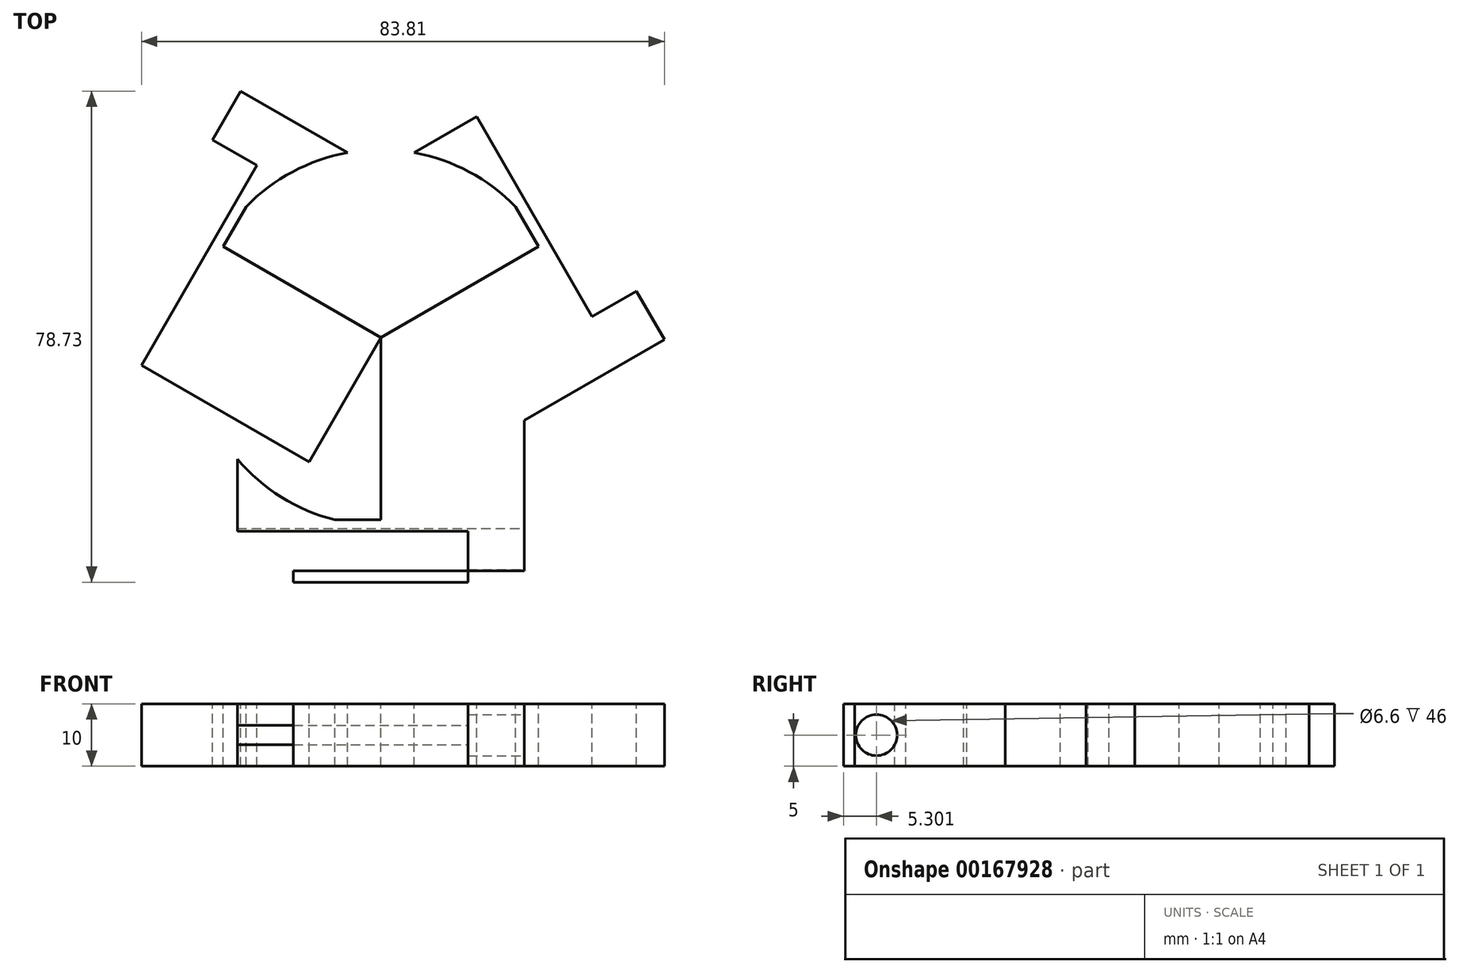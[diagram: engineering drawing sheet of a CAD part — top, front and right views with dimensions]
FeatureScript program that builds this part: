
annotation { "Feature Type Name" : "Feature", "Feature Type Description" : "" }
export const myFeature = defineFeature(function(context is Context, id is Id, definition is map)
    precondition{}
    {
        {
            var Q0;
            Q0=qCreatedBy(makeId("Top.planeOp"),FACE);
            var sketch = newSketch(context, id + "F0", { "sketchPlane" : qUnion([Q0])});
            skLineSegment(sketch, "E0", {"start": v(-23, -19.45) * mm, "end": v(-23, -31) * mm});
            skLineSegment(sketch, "E1", {"start": v(-23, -31) * mm, "end": v(-14, -31) * mm});
            skLineSegment(sketch, "E2", {"start": v(-14, -31) * mm, "end": v(-14, -29.2) * mm});
            skLineSegment(sketch, "E3", {"start": v(-23, -39.2) * mm, "end": v(-14, -39.2) * mm});
            skLineSegment(sketch, "E4", {"start": v(-14, -39.2) * mm, "end": v(-14, -37.4) * mm});
            skLineSegment(sketch, "E5", {"start": v(-14, -37.4) * mm, "end": v(-23, -37.4) * mm});
            skLineSegment(sketch, "E6", {"start": v(-23, -37.4) * mm, "end": v(-23, -39.2) * mm});
            skCircle(sketch, "E7", {"center": v(0, 0) * mm, "radius": 30.13 * mm});
            skLineSegment(sketch, "E8.bottom", {"start": v(-23, -39.2) * mm, "end": v(0, -39.2) * mm});
            skLineSegment(sketch, "E8.top", {"start": v(-23, 0) * mm, "end": v(0, 0) * mm});
            skLineSegment(sketch, "E8.left", {"start": v(-23, -39.2) * mm, "end": v(-23, 0) * mm});
            skLineSegment(sketch, "E8.right", {"start": v(0, -39.2) * mm, "end": v(0, 0) * mm});
            skLineSegment(sketch, "E9.bottom", {"start": v(-23, -31) * mm, "end": v(0, -31) * mm});
            skLineSegment(sketch, "E9.top", {"start": v(-23, -37.4) * mm, "end": v(0, -37.4) * mm});
            skLineSegment(sketch, "E9.left", {"start": v(-23, -31) * mm, "end": v(-23, -37.4) * mm});
            skLineSegment(sketch, "E9.right", {"start": v(0, -31) * mm, "end": v(0, -37.4) * mm});
            skLineSegment(sketch, "E10.bottom", {"start": v(-14, -29.2) * mm, "end": v(0, -29.2) * mm});
            skLineSegment(sketch, "E10.top", {"start": v(-14, -39.2) * mm, "end": v(0, -39.2) * mm});
            skLineSegment(sketch, "E10.left", {"start": v(-14, -29.2) * mm, "end": v(-14, -39.2) * mm});
            skLineSegment(sketch, "E10.right", {"start": v(0, -29.2) * mm, "end": v(0, -39.2) * mm});
            skLineSegment(sketch, "E11", {"start": v(-23, -34.2) * mm, "end": v(0, -34.2) * mm, "construction": true});
            skLineSegment(sketch, "E12.MirrorCS", {"start": v(23, -37.4) * mm, "end": v(23, -39.2) * mm});
            skLineSegment(sketch, "E13.MirrorCS", {"start": v(14, -39.2) * mm, "end": v(14, -37.4) * mm});
            skLineSegment(sketch, "E14.MirrorCS", {"start": v(14, -31) * mm, "end": v(14, -29.2) * mm});
            skLineSegment(sketch, "E15.MirrorCS", {"start": v(23, -31) * mm, "end": v(14, -31) * mm});
            skLineSegment(sketch, "E16.MirrorCS", {"start": v(23, -39.2) * mm, "end": v(14, -39.2) * mm});
            skLineSegment(sketch, "E17.MirrorCS", {"start": v(23, -31) * mm, "end": v(23, -37.4) * mm});
            skLineSegment(sketch, "E18.MirrorCS", {"start": v(23, -19.45) * mm, "end": v(23, -31) * mm});
            skLineSegment(sketch, "E19.MirrorCS", {"start": v(14, -37.4) * mm, "end": v(23, -37.4) * mm});
            skLineSegment(sketch, "E20.MirrorCS", {"start": v(14, -29.2) * mm, "end": v(14, -39.2) * mm});
            skLineSegment(sketch, "E21.MirrorCS", {"start": v(23, -39.2) * mm, "end": v(0, -39.2) * mm});
            skLineSegment(sketch, "E22.MirrorCS", {"start": v(23, 0) * mm, "end": v(0, 0) * mm});
            skLineSegment(sketch, "E23.MirrorCS", {"start": v(23, -37.4) * mm, "end": v(0, -37.4) * mm});
            skLineSegment(sketch, "E24.MirrorCS", {"start": v(23, -34.2) * mm, "end": v(0, -34.2) * mm, "construction": true});
            skLineSegment(sketch, "E25.MirrorCS", {"start": v(14, -39.2) * mm, "end": v(0, -39.2) * mm});
            skLineSegment(sketch, "E26.MirrorCS", {"start": v(14, -29.2) * mm, "end": v(0, -29.2) * mm});
            skLineSegment(sketch, "E27.MirrorCS", {"start": v(23, -31) * mm, "end": v(0, -31) * mm});
            skLineSegment(sketch, "E28.MirrorCS", {"start": v(23, -39.2) * mm, "end": v(23, 0) * mm});
            skLineSegment(sketch, "E29.1.0", {"start": v(33.96, 19.6) * mm, "end": v(0, 0) * mm});
            skLineSegment(sketch, "E29.1.1", {"start": v(20.9, 38.62) * mm, "end": v(32.4, 18.7) * mm});
            skLineSegment(sketch, "E29.1.2", {"start": v(22.46, 39.52) * mm, "end": v(26.96, 31.73) * mm});
            skLineSegment(sketch, "E29.1.3", {"start": v(32.3, 2.48) * mm, "end": v(40.96, 7.48) * mm});
            skLineSegment(sketch, "E29.1.4", {"start": v(-11.5, 19.92) * mm, "end": v(0, 0) * mm});
            skLineSegment(sketch, "E29.1.5", {"start": v(15.35, 35.42) * mm, "end": v(19.85, 27.63) * mm});
            skLineSegment(sketch, "E29.1.6", {"start": v(18.3, 26.73) * mm, "end": v(25.3, 14.6) * mm});
            skLineSegment(sketch, "E29.1.7", {"start": v(40.96, 7.48) * mm, "end": v(33.96, 19.6) * mm});
            skLineSegment(sketch, "E29.1.8", {"start": v(22.46, 39.52) * mm, "end": v(33.96, 19.6) * mm});
            skLineSegment(sketch, "E29.1.9", {"start": v(5.34, 29.64) * mm, "end": v(15.35, 35.42) * mm});
            skLineSegment(sketch, "E29.1.10", {"start": v(22.46, 39.52) * mm, "end": v(-11.5, 19.92) * mm});
            skLineSegment(sketch, "E29.1.11", {"start": v(32.3, 2.48) * mm, "end": v(25.3, 14.6) * mm});
            skLineSegment(sketch, "E29.1.12", {"start": v(18.3, 26.73) * mm, "end": v(26.96, 31.73) * mm});
            skLineSegment(sketch, "E29.1.13", {"start": v(15.35, 35.42) * mm, "end": v(26.85, 15.5) * mm});
            skLineSegment(sketch, "E29.1.14", {"start": v(18.13, 37.02) * mm, "end": v(29.63, 17.1) * mm, "construction": true});
            skLineSegment(sketch, "E29.1.15", {"start": v(41.13, -2.81) * mm, "end": v(29.63, 17.1) * mm, "construction": true});
            skLineSegment(sketch, "E29.1.16", {"start": v(38.35, -4.41) * mm, "end": v(26.85, 15.5) * mm});
            skLineSegment(sketch, "E29.1.17", {"start": v(45.46, -0.31) * mm, "end": v(11.5, -19.92) * mm});
            skLineSegment(sketch, "E29.1.18", {"start": v(11.5, -19.92) * mm, "end": v(0, 0) * mm});
            skLineSegment(sketch, "E29.1.19", {"start": v(45.46, -0.31) * mm, "end": v(33.96, 19.6) * mm});
            skLineSegment(sketch, "E29.1.20", {"start": v(39.4, 6.58) * mm, "end": v(43.9, -1.21) * mm});
            skLineSegment(sketch, "E29.1.21", {"start": v(43.9, -1.21) * mm, "end": v(32.4, 18.7) * mm});
            skLineSegment(sketch, "E29.1.22", {"start": v(25.4, 30.83) * mm, "end": v(20.9, 38.62) * mm});
            skLineSegment(sketch, "E29.1.23", {"start": v(18.3, 26.73) * mm, "end": v(25.3, 14.6) * mm});
            skLineSegment(sketch, "E29.1.24", {"start": v(-11.5, 19.92) * mm, "end": v(0, 0) * mm});
            skLineSegment(sketch, "E29.1.25", {"start": v(15.35, 35.42) * mm, "end": v(19.85, 27.63) * mm});
            skLineSegment(sketch, "E29.1.26", {"start": v(26.96, 31.73) * mm, "end": v(33.96, 19.6) * mm});
            skLineSegment(sketch, "E29.1.27", {"start": v(22.46, 39.52) * mm, "end": v(33.96, 19.6) * mm});
            skLineSegment(sketch, "E29.1.28", {"start": v(5.34, 29.64) * mm, "end": v(15.35, 35.42) * mm});
            skLineSegment(sketch, "E29.1.29", {"start": v(22.46, 39.52) * mm, "end": v(-11.5, 19.92) * mm});
            skLineSegment(sketch, "E29.1.30", {"start": v(33.96, 19.6) * mm, "end": v(0, 0) * mm});
            skLineSegment(sketch, "E29.1.31", {"start": v(45.46, -0.31) * mm, "end": v(40.96, 7.48) * mm});
            skLineSegment(sketch, "E29.1.32", {"start": v(38.35, -4.41) * mm, "end": v(33.85, 3.38) * mm});
            skLineSegment(sketch, "E29.1.33", {"start": v(28.34, -10.2) * mm, "end": v(38.35, -4.41) * mm});
            skLineSegment(sketch, "E29.1.34", {"start": v(38.35, -4.41) * mm, "end": v(43.9, -1.21) * mm});
            skLineSegment(sketch, "E29.1.35", {"start": v(18.13, 37.02) * mm, "end": v(29.63, 17.1) * mm, "construction": true});
            skLineSegment(sketch, "E29.1.36", {"start": v(18.3, 26.73) * mm, "end": v(26.96, 31.73) * mm});
            skLineSegment(sketch, "E29.1.37", {"start": v(20.9, 38.62) * mm, "end": v(32.4, 18.7) * mm});
            skLineSegment(sketch, "E29.1.38", {"start": v(15.35, 35.42) * mm, "end": v(26.85, 15.5) * mm});
            skLineSegment(sketch, "E29.1.39", {"start": v(20.9, 38.62) * mm, "end": v(32.4, 18.7) * mm});
            skLineSegment(sketch, "E29.1.40", {"start": v(18.3, 26.73) * mm, "end": v(25.3, 14.6) * mm});
            skLineSegment(sketch, "E29.1.41", {"start": v(-11.5, 19.92) * mm, "end": v(0, 0) * mm});
            skLineSegment(sketch, "E29.1.42", {"start": v(15.35, 35.42) * mm, "end": v(19.85, 27.63) * mm});
            skLineSegment(sketch, "E29.1.43", {"start": v(5.34, 29.64) * mm, "end": v(15.35, 35.42) * mm});
            skLineSegment(sketch, "E29.1.44", {"start": v(22.46, 39.52) * mm, "end": v(-11.5, 19.92) * mm});
            skLineSegment(sketch, "E29.1.45", {"start": v(26.96, 31.73) * mm, "end": v(33.96, 19.6) * mm});
            skLineSegment(sketch, "E29.1.46", {"start": v(18.13, 37.02) * mm, "end": v(29.63, 17.1) * mm, "construction": true});
            skLineSegment(sketch, "E29.1.47", {"start": v(18.3, 26.73) * mm, "end": v(26.96, 31.73) * mm});
            skLineSegment(sketch, "E29.1.48", {"start": v(15.35, 35.42) * mm, "end": v(26.85, 15.5) * mm});
            skLineSegment(sketch, "E29.1.49", {"start": v(33.96, 19.6) * mm, "end": v(0, 0) * mm});
            skLineSegment(sketch, "E29.1.50", {"start": v(25.4, 30.83) * mm, "end": v(20.9, 38.62) * mm});
            skLineSegment(sketch, "E29.1.51", {"start": v(22.46, 39.52) * mm, "end": v(26.96, 31.73) * mm});
            skLineSegment(sketch, "E29.1.52", {"start": v(25.4, 30.83) * mm, "end": v(20.9, 38.62) * mm});
            skLineSegment(sketch, "E29.1.53", {"start": v(22.46, 39.52) * mm, "end": v(26.96, 31.73) * mm});
            skLineSegment(sketch, "E29.1.54", {"start": v(33.96, 19.6) * mm, "end": v(0, 0) * mm});
            skLineSegment(sketch, "E29.1.55", {"start": v(26.96, 31.73) * mm, "end": v(33.96, 19.6) * mm});
            skLineSegment(sketch, "E29.1.56", {"start": v(22.46, 39.52) * mm, "end": v(-11.5, 19.92) * mm});
            skLineSegment(sketch, "E29.1.57", {"start": v(-11.5, 19.92) * mm, "end": v(0, 0) * mm});
            skLineSegment(sketch, "E29.1.58", {"start": v(15.35, 35.42) * mm, "end": v(19.85, 27.63) * mm});
            skLineSegment(sketch, "E29.1.59", {"start": v(18.3, 26.73) * mm, "end": v(25.3, 14.6) * mm});
            skLineSegment(sketch, "E29.1.60", {"start": v(33.85, 3.38) * mm, "end": v(32.3, 2.48) * mm});
            skLineSegment(sketch, "E29.1.61", {"start": v(15.35, 35.42) * mm, "end": v(26.85, 15.5) * mm});
            skLineSegment(sketch, "E29.1.62", {"start": v(18.13, 37.02) * mm, "end": v(29.63, 17.1) * mm, "construction": true});
            skLineSegment(sketch, "E29.1.63", {"start": v(18.3, 26.73) * mm, "end": v(26.96, 31.73) * mm});
            skLineSegment(sketch, "E29.1.64", {"start": v(20.9, 38.62) * mm, "end": v(32.4, 18.7) * mm});
            skLineSegment(sketch, "E29.1.65", {"start": v(22.46, 39.52) * mm, "end": v(33.96, 19.6) * mm});
            skLineSegment(sketch, "E29.1.66", {"start": v(15.35, 35.42) * mm, "end": v(20.9, 38.62) * mm});
            skLineSegment(sketch, "E29.1.67", {"start": v(5.34, 29.64) * mm, "end": v(15.35, 35.42) * mm});
            skLineSegment(sketch, "E29.1.68", {"start": v(43.9, -1.21) * mm, "end": v(45.46, -0.31) * mm});
            skLineSegment(sketch, "E29.1.69", {"start": v(40.96, 7.48) * mm, "end": v(39.4, 6.58) * mm});
            skLineSegment(sketch, "E29.1.70", {"start": v(25.4, 30.83) * mm, "end": v(20.9, 38.62) * mm});
            skLineSegment(sketch, "E29.1.71", {"start": v(33.96, 19.6) * mm, "end": v(0, 0) * mm});
            skLineSegment(sketch, "E29.1.72", {"start": v(26.85, 15.5) * mm, "end": v(32.4, 18.7) * mm});
            skLineSegment(sketch, "E29.1.73", {"start": v(26.96, 31.73) * mm, "end": v(33.96, 19.6) * mm});
            skLineSegment(sketch, "E29.1.74", {"start": v(22.46, 39.52) * mm, "end": v(33.96, 19.6) * mm});
            skLineSegment(sketch, "E29.1.75", {"start": v(15.35, 35.42) * mm, "end": v(20.9, 38.62) * mm});
            skLineSegment(sketch, "E29.1.76", {"start": v(26.85, 15.5) * mm, "end": v(32.4, 18.7) * mm});
            skLineSegment(sketch, "E29.1.77", {"start": v(15.35, 35.42) * mm, "end": v(20.9, 38.62) * mm});
            skLineSegment(sketch, "E29.1.78", {"start": v(22.46, 39.52) * mm, "end": v(26.96, 31.73) * mm});
            skLineSegment(sketch, "E29.1.79", {"start": v(25.3, 14.6) * mm, "end": v(33.96, 19.6) * mm});
            skLineSegment(sketch, "E29.1.80", {"start": v(15.35, 35.42) * mm, "end": v(20.9, 38.62) * mm});
            skLineSegment(sketch, "E29.1.81", {"start": v(26.85, 15.5) * mm, "end": v(32.4, 18.7) * mm});
            skLineSegment(sketch, "E29.1.82", {"start": v(25.3, 14.6) * mm, "end": v(33.96, 19.6) * mm});
            skLineSegment(sketch, "E29.1.83", {"start": v(26.85, 15.5) * mm, "end": v(32.4, 18.7) * mm});
            skLineSegment(sketch, "E29.1.84", {"start": v(25.3, 14.6) * mm, "end": v(33.96, 19.6) * mm});
            skLineSegment(sketch, "E29.1.85", {"start": v(26.85, 15.5) * mm, "end": v(32.4, 18.7) * mm});
            skLineSegment(sketch, "E29.1.86", {"start": v(25.3, 14.6) * mm, "end": v(33.96, 19.6) * mm});
            skLineSegment(sketch, "E29.1.87", {"start": v(19.85, 27.63) * mm, "end": v(18.3, 26.73) * mm});
            skLineSegment(sketch, "E29.1.88", {"start": v(25.3, 14.6) * mm, "end": v(33.96, 19.6) * mm});
            skLineSegment(sketch, "E29.1.89", {"start": v(19.85, 27.63) * mm, "end": v(18.3, 26.73) * mm});
            skLineSegment(sketch, "E29.1.90", {"start": v(19.85, 27.63) * mm, "end": v(18.3, 26.73) * mm});
            skLineSegment(sketch, "E29.1.91", {"start": v(19.85, 27.63) * mm, "end": v(18.3, 26.73) * mm});
            skLineSegment(sketch, "E29.1.92", {"start": v(26.96, 31.73) * mm, "end": v(25.4, 30.83) * mm});
            skLineSegment(sketch, "E29.1.93", {"start": v(20.9, 38.62) * mm, "end": v(22.46, 39.52) * mm});
            skLineSegment(sketch, "E29.1.94", {"start": v(20.9, 38.62) * mm, "end": v(22.46, 39.52) * mm});
            skLineSegment(sketch, "E29.1.95", {"start": v(26.96, 31.73) * mm, "end": v(25.4, 30.83) * mm});
            skLineSegment(sketch, "E29.1.96", {"start": v(20.9, 38.62) * mm, "end": v(22.46, 39.52) * mm});
            skLineSegment(sketch, "E29.1.97", {"start": v(26.96, 31.73) * mm, "end": v(25.4, 30.83) * mm});
            skLineSegment(sketch, "E29.1.98", {"start": v(20.9, 38.62) * mm, "end": v(22.46, 39.52) * mm});
            skLineSegment(sketch, "E29.1.99", {"start": v(26.96, 31.73) * mm, "end": v(25.4, 30.83) * mm});
            skLineSegment(sketch, "E29.2.0", {"start": v(-33.96, 19.6) * mm, "end": v(0, 0) * mm});
            skLineSegment(sketch, "E29.2.1", {"start": v(-43.9, -1.21) * mm, "end": v(-32.4, 18.7) * mm});
            skLineSegment(sketch, "E29.2.2", {"start": v(-45.46, -0.31) * mm, "end": v(-40.96, 7.48) * mm});
            skLineSegment(sketch, "E29.2.3", {"start": v(-18.3, 26.73) * mm, "end": v(-26.96, 31.73) * mm});
            skLineSegment(sketch, "E29.2.4", {"start": v(-11.5, -19.92) * mm, "end": v(0, 0) * mm});
            skLineSegment(sketch, "E29.2.5", {"start": v(-38.35, -4.41) * mm, "end": v(-33.85, 3.38) * mm});
            skLineSegment(sketch, "E29.2.6", {"start": v(-32.3, 2.48) * mm, "end": v(-25.3, 14.6) * mm});
            skLineSegment(sketch, "E29.2.7", {"start": v(-26.96, 31.73) * mm, "end": v(-33.96, 19.6) * mm});
            skLineSegment(sketch, "E29.2.8", {"start": v(-45.46, -0.31) * mm, "end": v(-33.96, 19.6) * mm});
            skLineSegment(sketch, "E29.2.9", {"start": v(-28.34, -10.2) * mm, "end": v(-38.35, -4.41) * mm});
            skLineSegment(sketch, "E29.2.10", {"start": v(-45.46, -0.31) * mm, "end": v(-11.5, -19.92) * mm});
            skLineSegment(sketch, "E29.2.11", {"start": v(-18.3, 26.73) * mm, "end": v(-25.3, 14.6) * mm});
            skLineSegment(sketch, "E29.2.12", {"start": v(-32.3, 2.48) * mm, "end": v(-40.96, 7.48) * mm});
            skLineSegment(sketch, "E29.2.13", {"start": v(-38.35, -4.41) * mm, "end": v(-26.85, 15.5) * mm});
            skLineSegment(sketch, "E29.2.14", {"start": v(-41.13, -2.81) * mm, "end": v(-29.63, 17.1) * mm, "construction": true});
            skLineSegment(sketch, "E29.2.15", {"start": v(-18.13, 37.02) * mm, "end": v(-29.63, 17.1) * mm, "construction": true});
            skLineSegment(sketch, "E29.2.16", {"start": v(-15.35, 35.42) * mm, "end": v(-26.85, 15.5) * mm});
            skLineSegment(sketch, "E29.2.17", {"start": v(-22.46, 39.52) * mm, "end": v(11.5, 19.92) * mm});
            skLineSegment(sketch, "E29.2.18", {"start": v(11.5, 19.92) * mm, "end": v(0, 0) * mm});
            skLineSegment(sketch, "E29.2.19", {"start": v(-22.46, 39.52) * mm, "end": v(-33.96, 19.6) * mm});
            skLineSegment(sketch, "E29.2.20", {"start": v(-25.4, 30.83) * mm, "end": v(-20.9, 38.62) * mm});
            skLineSegment(sketch, "E29.2.21", {"start": v(-20.9, 38.62) * mm, "end": v(-32.4, 18.7) * mm});
            skLineSegment(sketch, "E29.2.22", {"start": v(-39.4, 6.58) * mm, "end": v(-43.9, -1.21) * mm});
            skLineSegment(sketch, "E29.2.23", {"start": v(-32.3, 2.48) * mm, "end": v(-25.3, 14.6) * mm});
            skLineSegment(sketch, "E29.2.24", {"start": v(-11.5, -19.92) * mm, "end": v(0, 0) * mm});
            skLineSegment(sketch, "E29.2.25", {"start": v(-38.35, -4.41) * mm, "end": v(-33.85, 3.38) * mm});
            skLineSegment(sketch, "E29.2.26", {"start": v(-40.96, 7.48) * mm, "end": v(-33.96, 19.6) * mm});
            skLineSegment(sketch, "E29.2.27", {"start": v(-45.46, -0.31) * mm, "end": v(-33.96, 19.6) * mm});
            skLineSegment(sketch, "E29.2.28", {"start": v(-28.34, -10.2) * mm, "end": v(-38.35, -4.41) * mm});
            skLineSegment(sketch, "E29.2.29", {"start": v(-45.46, -0.31) * mm, "end": v(-11.5, -19.92) * mm});
            skLineSegment(sketch, "E29.2.30", {"start": v(-33.96, 19.6) * mm, "end": v(0, 0) * mm});
            skLineSegment(sketch, "E29.2.31", {"start": v(-22.46, 39.52) * mm, "end": v(-26.96, 31.73) * mm});
            skLineSegment(sketch, "E29.2.32", {"start": v(-15.35, 35.42) * mm, "end": v(-19.85, 27.63) * mm});
            skLineSegment(sketch, "E29.2.33", {"start": v(-5.34, 29.64) * mm, "end": v(-15.35, 35.42) * mm});
            skLineSegment(sketch, "E29.2.34", {"start": v(-15.35, 35.42) * mm, "end": v(-20.9, 38.62) * mm});
            skLineSegment(sketch, "E29.2.35", {"start": v(-41.13, -2.81) * mm, "end": v(-29.63, 17.1) * mm, "construction": true});
            skLineSegment(sketch, "E29.2.36", {"start": v(-32.3, 2.48) * mm, "end": v(-40.96, 7.48) * mm});
            skLineSegment(sketch, "E29.2.37", {"start": v(-43.9, -1.21) * mm, "end": v(-32.4, 18.7) * mm});
            skLineSegment(sketch, "E29.2.38", {"start": v(-38.35, -4.41) * mm, "end": v(-26.85, 15.5) * mm});
            skLineSegment(sketch, "E29.2.39", {"start": v(-43.9, -1.21) * mm, "end": v(-32.4, 18.7) * mm});
            skLineSegment(sketch, "E29.2.40", {"start": v(-32.3, 2.48) * mm, "end": v(-25.3, 14.6) * mm});
            skLineSegment(sketch, "E29.2.41", {"start": v(-11.5, -19.92) * mm, "end": v(0, 0) * mm});
            skLineSegment(sketch, "E29.2.42", {"start": v(-38.35, -4.41) * mm, "end": v(-33.85, 3.38) * mm});
            skLineSegment(sketch, "E29.2.43", {"start": v(-28.34, -10.2) * mm, "end": v(-38.35, -4.41) * mm});
            skLineSegment(sketch, "E29.2.44", {"start": v(-45.46, -0.31) * mm, "end": v(-11.5, -19.92) * mm});
            skLineSegment(sketch, "E29.2.45", {"start": v(-40.96, 7.48) * mm, "end": v(-33.96, 19.6) * mm});
            skLineSegment(sketch, "E29.2.46", {"start": v(-41.13, -2.81) * mm, "end": v(-29.63, 17.1) * mm, "construction": true});
            skLineSegment(sketch, "E29.2.47", {"start": v(-32.3, 2.48) * mm, "end": v(-40.96, 7.48) * mm});
            skLineSegment(sketch, "E29.2.48", {"start": v(-38.35, -4.41) * mm, "end": v(-26.85, 15.5) * mm});
            skLineSegment(sketch, "E29.2.49", {"start": v(-33.96, 19.6) * mm, "end": v(0, 0) * mm});
            skLineSegment(sketch, "E29.2.50", {"start": v(-39.4, 6.58) * mm, "end": v(-43.9, -1.21) * mm});
            skLineSegment(sketch, "E29.2.51", {"start": v(-45.46, -0.31) * mm, "end": v(-40.96, 7.48) * mm});
            skLineSegment(sketch, "E29.2.52", {"start": v(-39.4, 6.58) * mm, "end": v(-43.9, -1.21) * mm});
            skLineSegment(sketch, "E29.2.53", {"start": v(-45.46, -0.31) * mm, "end": v(-40.96, 7.48) * mm});
            skLineSegment(sketch, "E29.2.54", {"start": v(-33.96, 19.6) * mm, "end": v(0, 0) * mm});
            skLineSegment(sketch, "E29.2.55", {"start": v(-40.96, 7.48) * mm, "end": v(-33.96, 19.6) * mm});
            skLineSegment(sketch, "E29.2.56", {"start": v(-45.46, -0.31) * mm, "end": v(-11.5, -19.92) * mm});
            skLineSegment(sketch, "E29.2.57", {"start": v(-11.5, -19.92) * mm, "end": v(0, 0) * mm});
            skLineSegment(sketch, "E29.2.58", {"start": v(-38.35, -4.41) * mm, "end": v(-33.85, 3.38) * mm});
            skLineSegment(sketch, "E29.2.59", {"start": v(-32.3, 2.48) * mm, "end": v(-25.3, 14.6) * mm});
            skLineSegment(sketch, "E29.2.60", {"start": v(-19.85, 27.63) * mm, "end": v(-18.3, 26.73) * mm});
            skLineSegment(sketch, "E29.2.61", {"start": v(-38.35, -4.41) * mm, "end": v(-26.85, 15.5) * mm});
            skLineSegment(sketch, "E29.2.62", {"start": v(-41.13, -2.81) * mm, "end": v(-29.63, 17.1) * mm, "construction": true});
            skLineSegment(sketch, "E29.2.63", {"start": v(-32.3, 2.48) * mm, "end": v(-40.96, 7.48) * mm});
            skLineSegment(sketch, "E29.2.64", {"start": v(-43.9, -1.21) * mm, "end": v(-32.4, 18.7) * mm});
            skLineSegment(sketch, "E29.2.65", {"start": v(-45.46, -0.31) * mm, "end": v(-33.96, 19.6) * mm});
            skLineSegment(sketch, "E29.2.66", {"start": v(-38.35, -4.41) * mm, "end": v(-43.9, -1.21) * mm});
            skLineSegment(sketch, "E29.2.67", {"start": v(-28.34, -10.2) * mm, "end": v(-38.35, -4.41) * mm});
            skLineSegment(sketch, "E29.2.68", {"start": v(-20.9, 38.62) * mm, "end": v(-22.46, 39.52) * mm});
            skLineSegment(sketch, "E29.2.69", {"start": v(-26.96, 31.73) * mm, "end": v(-25.4, 30.83) * mm});
            skLineSegment(sketch, "E29.2.70", {"start": v(-39.4, 6.58) * mm, "end": v(-43.9, -1.21) * mm});
            skLineSegment(sketch, "E29.2.71", {"start": v(-33.96, 19.6) * mm, "end": v(0, 0) * mm});
            skLineSegment(sketch, "E29.2.72", {"start": v(-26.85, 15.5) * mm, "end": v(-32.4, 18.7) * mm});
            skLineSegment(sketch, "E29.2.73", {"start": v(-40.96, 7.48) * mm, "end": v(-33.96, 19.6) * mm});
            skLineSegment(sketch, "E29.2.74", {"start": v(-45.46, -0.31) * mm, "end": v(-33.96, 19.6) * mm});
            skLineSegment(sketch, "E29.2.75", {"start": v(-38.35, -4.41) * mm, "end": v(-43.9, -1.21) * mm});
            skLineSegment(sketch, "E29.2.76", {"start": v(-26.85, 15.5) * mm, "end": v(-32.4, 18.7) * mm});
            skLineSegment(sketch, "E29.2.77", {"start": v(-38.35, -4.41) * mm, "end": v(-43.9, -1.21) * mm});
            skLineSegment(sketch, "E29.2.78", {"start": v(-45.46, -0.31) * mm, "end": v(-40.96, 7.48) * mm});
            skLineSegment(sketch, "E29.2.79", {"start": v(-25.3, 14.6) * mm, "end": v(-33.96, 19.6) * mm});
            skLineSegment(sketch, "E29.2.80", {"start": v(-38.35, -4.41) * mm, "end": v(-43.9, -1.21) * mm});
            skLineSegment(sketch, "E29.2.81", {"start": v(-26.85, 15.5) * mm, "end": v(-32.4, 18.7) * mm});
            skLineSegment(sketch, "E29.2.82", {"start": v(-25.3, 14.6) * mm, "end": v(-33.96, 19.6) * mm});
            skLineSegment(sketch, "E29.2.83", {"start": v(-26.85, 15.5) * mm, "end": v(-32.4, 18.7) * mm});
            skLineSegment(sketch, "E29.2.84", {"start": v(-25.3, 14.6) * mm, "end": v(-33.96, 19.6) * mm});
            skLineSegment(sketch, "E29.2.85", {"start": v(-26.85, 15.5) * mm, "end": v(-32.4, 18.7) * mm});
            skLineSegment(sketch, "E29.2.86", {"start": v(-25.3, 14.6) * mm, "end": v(-33.96, 19.6) * mm});
            skLineSegment(sketch, "E29.2.87", {"start": v(-33.85, 3.38) * mm, "end": v(-32.3, 2.48) * mm});
            skLineSegment(sketch, "E29.2.88", {"start": v(-25.3, 14.6) * mm, "end": v(-33.96, 19.6) * mm});
            skLineSegment(sketch, "E29.2.89", {"start": v(-33.85, 3.38) * mm, "end": v(-32.3, 2.48) * mm});
            skLineSegment(sketch, "E29.2.90", {"start": v(-33.85, 3.38) * mm, "end": v(-32.3, 2.48) * mm});
            skLineSegment(sketch, "E29.2.91", {"start": v(-33.85, 3.38) * mm, "end": v(-32.3, 2.48) * mm});
            skLineSegment(sketch, "E29.2.92", {"start": v(-40.96, 7.48) * mm, "end": v(-39.4, 6.58) * mm});
            skLineSegment(sketch, "E29.2.93", {"start": v(-43.9, -1.21) * mm, "end": v(-45.46, -0.31) * mm});
            skLineSegment(sketch, "E29.2.94", {"start": v(-43.9, -1.21) * mm, "end": v(-45.46, -0.31) * mm});
            skLineSegment(sketch, "E29.2.95", {"start": v(-40.96, 7.48) * mm, "end": v(-39.4, 6.58) * mm});
            skLineSegment(sketch, "E29.2.96", {"start": v(-43.9, -1.21) * mm, "end": v(-45.46, -0.31) * mm});
            skLineSegment(sketch, "E29.2.97", {"start": v(-40.96, 7.48) * mm, "end": v(-39.4, 6.58) * mm});
            skLineSegment(sketch, "E29.2.98", {"start": v(-43.9, -1.21) * mm, "end": v(-45.46, -0.31) * mm});
            skLineSegment(sketch, "E29.2.99", {"start": v(-40.96, 7.48) * mm, "end": v(-39.4, 6.58) * mm});
            skSolve(sketch);
        }
        {
            var Q0;
            {var subQ0=sQuery(id+"F0.wireOp",EDGE,"E29.1.67");var subQ3=sQuery(id+"F0.wireOp",EDGE,"E7");var subQ4=makeQuery(id+"F0.imprint","INTERSECT",VERTEX,{"derivedFrom":[subQ3,subQ0]});Q0=makeQuery(id+"F0.imprint","IMPRINT",FACE,{"disambiguationData":[TD([[makeQuery(id+"F0.imprint","IMPRINT",EDGE,{"disambiguationData":[TD([[subQ4,-1.0]])],"derivedFrom":subQ3}),1.0]])]});}
            var Q1;
            {var subQ3=sQuery(id+"F0.wireOp",EDGE,"E8.left");var subQ5=makeQuery(id+"F0.imprint","IMPRINT",VERTEX,{"derivedFrom":subQ3});Q1=makeQuery(id+"F0.imprint","IMPRINT",FACE,{"disambiguationData":[TD([[makeQuery(id+"F0.imprint","IMPRINT",EDGE,{"disambiguationData":[TD([[subQ5,1.0]])],"derivedFrom":subQ3}),1.0]])]});}
            var Q2;
            {var subQ0=sQuery(id+"F0.wireOp",EDGE,"E28.MirrorCS");var subQ1=makeQuery(id+"F0.imprint","IMPRINT",VERTEX,{"derivedFrom":subQ0});Q2=makeQuery(id+"F0.imprint","IMPRINT",FACE,{"disambiguationData":[TD([[makeQuery(id+"F0.imprint","IMPRINT",EDGE,{"disambiguationData":[TD([[subQ1,1.0]])],"derivedFrom":subQ0}),-1.0]])]});}
            var Q3;
            {var subQ0=sQuery(id+"F0.wireOp",EDGE,"E8.bottom");Q3=makeQuery(id+"F0.imprint","IMPRINT",FACE,{"disambiguationData":[TD([[makeQuery(id+"F0.imprint","IMPRINT",EDGE,{"derivedFrom":subQ0}),1.0]])]});}
            var Q4;
            {var subQ0=sQuery(id+"F0.wireOp",EDGE,"E21.MirrorCS");Q4=makeQuery(id+"F0.imprint","IMPRINT",FACE,{"disambiguationData":[TD([[makeQuery(id+"F0.imprint","IMPRINT",EDGE,{"derivedFrom":subQ0}),-1.0]])]});}
            var Q5;
            Q5=makeQuery(id+"F0.imprint","IMPRINT",FACE,{"disambiguationData":[TD([[makeQuery(id+"F0.imprint","IMPRINT",EDGE,{"derivedFrom":sQuery(id+"F0.wireOp",EDGE,"E29.1.31")}),1.0]])]});
            var Q6;
            Q6=makeQuery(id+"F0.imprint","IMPRINT",FACE,{"disambiguationData":[TD([[makeQuery(id+"F0.imprint","IMPRINT",EDGE,{"derivedFrom":sQuery(id+"F0.wireOp",EDGE,"E29.1.70")}),-1.0]])]});
            var Q7;
            Q7=makeQuery(id+"F0.imprint","IMPRINT",FACE,{"disambiguationData":[TD([[makeQuery(id+"F0.imprint","IMPRINT",EDGE,{"derivedFrom":sQuery(id+"F0.wireOp",EDGE,"E29.2.31")}),1.0]])]});
            var Q8;
            Q8=makeQuery(id+"F0.imprint","IMPRINT",FACE,{"disambiguationData":[TD([[makeQuery(id+"F0.imprint","IMPRINT",EDGE,{"derivedFrom":sQuery(id+"F0.wireOp",EDGE,"E29.2.70")}),-1.0]])]});
            var Q9;
            {var subQ5=sQuery(id+"F0.wireOp",EDGE,"E29.1.91");Q9=makeQuery(id+"F0.imprint","IMPRINT",FACE,{"disambiguationData":[TD([[makeQuery(id+"F0.imprint","IMPRINT",EDGE,{"derivedFrom":subQ5}),-1.0]])]});}
            var Q10;
            {var subQ1=sQuery(id+"F0.wireOp",EDGE,"E29.2.32");Q10=makeQuery(id+"F0.imprint","IMPRINT",FACE,{"disambiguationData":[TD([[makeQuery(id+"F0.imprint","IMPRINT",EDGE,{"derivedFrom":subQ1}),1.0]])]});}
            var Q11;
            {var subQ5=sQuery(id+"F0.wireOp",EDGE,"E29.2.91");Q11=makeQuery(id+"F0.imprint","IMPRINT",FACE,{"disambiguationData":[TD([[makeQuery(id+"F0.imprint","IMPRINT",EDGE,{"derivedFrom":subQ5}),-1.0]])]});}
            var Q12;
            {var subQ3=sQuery(id+"F0.wireOp",EDGE,"E7");var subQ6=sQuery(id+"F0.wireOp",EDGE,"E8.left");var subQ9=makeQuery(id+"F0.imprint","INTERSECT",VERTEX,{"derivedFrom":[subQ3,subQ6]});Q12=makeQuery(id+"F0.imprint","IMPRINT",FACE,{"disambiguationData":[TD([[makeQuery(id+"F0.imprint","IMPRINT",EDGE,{"disambiguationData":[TD([[subQ9,-1.0]])],"derivedFrom":subQ3}),-1.0]])]});}
            var Q13;
            {var subQ3=sQuery(id+"F0.wireOp",EDGE,"E7");var subQ5=sQuery(id+"F0.wireOp",EDGE,"E28.MirrorCS");var subQ9=makeQuery(id+"F0.imprint","INTERSECT",VERTEX,{"derivedFrom":[subQ3,subQ5]});Q13=makeQuery(id+"F0.imprint","IMPRINT",FACE,{"disambiguationData":[TD([[makeQuery(id+"F0.imprint","IMPRINT",EDGE,{"disambiguationData":[TD([[subQ9,1.0]])],"derivedFrom":subQ3}),-1.0]])]});}
            var Q14;
            {var subQ1=sQuery(id+"F0.wireOp",EDGE,"E29.1.32");Q14=makeQuery(id+"F0.imprint","IMPRINT",FACE,{"disambiguationData":[TD([[makeQuery(id+"F0.imprint","IMPRINT",EDGE,{"derivedFrom":subQ1}),1.0]])]});}
            var Q15;
            {var subQ0=sQuery(id+"F0.wireOp",EDGE,"E9.left");Q15=makeQuery(id+"F0.imprint","IMPRINT",FACE,{"disambiguationData":[TD([[makeQuery(id+"F0.imprint","IMPRINT",EDGE,{"derivedFrom":subQ0}),1.0]])]});}
            var Q16;
            {var subQ0=sQuery(id+"F0.wireOp",EDGE,"E27.MirrorCS");var subQ1=sQuery(id+"F0.wireOp",EDGE,"E20.MirrorCS");var subQ2=makeQuery(id+"F0.imprint","INTERSECT",VERTEX,{"derivedFrom":[subQ1,subQ0]});Q16=makeQuery(id+"F0.imprint","IMPRINT",FACE,{"disambiguationData":[TD([[makeQuery(id+"F0.imprint","IMPRINT",EDGE,{"disambiguationData":[TD([[subQ2,-1.0]])],"derivedFrom":subQ1}),1.0]])]});}
            var Q17;
            {var subQ0=sQuery(id+"F0.wireOp",EDGE,"E29.1.3");Q17=makeQuery(id+"F0.imprint","IMPRINT",FACE,{"disambiguationData":[TD([[makeQuery(id+"F0.imprint","IMPRINT",EDGE,{"derivedFrom":subQ0}),-1.0]])]});}
            var Q18;
            {var subQ2=sQuery(id+"F0.wireOp",EDGE,"E29.1.63");Q18=makeQuery(id+"F0.imprint","IMPRINT",FACE,{"disambiguationData":[TD([[makeQuery(id+"F0.imprint","IMPRINT",EDGE,{"derivedFrom":subQ2}),1.0]])]});}
            var Q19;
            {var subQ0=sQuery(id+"F0.wireOp",EDGE,"E29.2.3");Q19=makeQuery(id+"F0.imprint","IMPRINT",FACE,{"disambiguationData":[TD([[makeQuery(id+"F0.imprint","IMPRINT",EDGE,{"derivedFrom":subQ0}),-1.0]])]});}
            var Q20;
            {var subQ2=sQuery(id+"F0.wireOp",EDGE,"E29.2.63");Q20=makeQuery(id+"F0.imprint","IMPRINT",FACE,{"disambiguationData":[TD([[makeQuery(id+"F0.imprint","IMPRINT",EDGE,{"derivedFrom":subQ2}),1.0]])]});}
            var Q21;
            {var subQ8=sQuery(id+"F0.wireOp",EDGE,"E29.1.71");Q21=makeQuery(id+"F0.imprint","IMPRINT",FACE,{"disambiguationData":[TD([[makeQuery(id+"F0.imprint","IMPRINT",EDGE,{"derivedFrom":subQ8}),-1.0]])]});}
            var Q22;
            {var subQ0=sQuery(id+"F0.wireOp",EDGE,"E8.top");Q22=makeQuery(id+"F0.imprint","IMPRINT",FACE,{"disambiguationData":[TD([[makeQuery(id+"F0.imprint","IMPRINT",EDGE,{"derivedFrom":subQ0}),1.0]])]});}
            var Q23;
            {var subQ9=sQuery(id+"F0.wireOp",EDGE,"E29.2.57");Q23=makeQuery(id+"F0.imprint","IMPRINT",FACE,{"disambiguationData":[TD([[makeQuery(id+"F0.imprint","IMPRINT",EDGE,{"derivedFrom":subQ9}),-1.0]])]});}
            var Q24;
            {var subQ4=sQuery(id+"F0.wireOp",EDGE,"E29.1.18");Q24=makeQuery(id+"F0.imprint","IMPRINT",FACE,{"disambiguationData":[TD([[makeQuery(id+"F0.imprint","IMPRINT",EDGE,{"derivedFrom":subQ4}),1.0]])]});}
            var Q25;
            {var subQ1=sQuery(id+"F0.wireOp",EDGE,"E22.MirrorCS");Q25=makeQuery(id+"F0.imprint","IMPRINT",FACE,{"disambiguationData":[TD([[makeQuery(id+"F0.imprint","IMPRINT",EDGE,{"derivedFrom":subQ1}),-1.0]])]});}
            var Q26;
            {var subQ4=sQuery(id+"F0.wireOp",EDGE,"E29.1.57");Q26=makeQuery(id+"F0.imprint","IMPRINT",FACE,{"disambiguationData":[TD([[makeQuery(id+"F0.imprint","IMPRINT",EDGE,{"derivedFrom":subQ4}),-1.0]])]});}
            var Q27;
            {var subQ0=sQuery(id+"F0.wireOp",EDGE,"E29.1.57");Q27=makeQuery(id+"F0.imprint","IMPRINT",FACE,{"disambiguationData":[TD([[makeQuery(id+"F0.imprint","IMPRINT",EDGE,{"derivedFrom":subQ0}),1.0]])]});}
            var Q28;
            {var subQ0=sQuery(id+"F0.wireOp",EDGE,"E8.top");Q28=makeQuery(id+"F0.imprint","IMPRINT",FACE,{"disambiguationData":[TD([[makeQuery(id+"F0.imprint","IMPRINT",EDGE,{"derivedFrom":subQ0}),-1.0]])]});}
            var Q29;
            {var subQ0=sQuery(id+"F0.wireOp",EDGE,"E22.MirrorCS");Q29=makeQuery(id+"F0.imprint","IMPRINT",FACE,{"disambiguationData":[TD([[makeQuery(id+"F0.imprint","IMPRINT",EDGE,{"derivedFrom":subQ0}),1.0]])]});}
            extrude(context, id + "F1", {"entities" : qUnion([Q0, Q1, Q2, Q3, Q4, Q5, Q6, Q7, Q8, Q9, Q10, Q11, Q12, Q13, Q14, Q15, Q16, Q17, Q18, Q19, Q20, Q21, Q22, Q23, Q24, Q25, Q26, Q27, Q28, Q29]), "oppositeDirection" : true, "depth" : 10 * mm});
        }
        {
            var Q0;
            Q0=makeQuery(id+"F1.opExtrude","SWEPT_FACE",FACE,{"disambiguationData":[OSD([sQuery(id+"F0.wireOp",EDGE,"E28.MirrorCS")])]});
            var sketch = newSketch(context, id + "F2", { "sketchPlane" : qUnion([Q0])});
            skLineSegment(sketch, "E30", {"start": v(-33.9, -10) * mm, "end": v(-33.9, 0) * mm});
            skPoint(sketch, "E31", {"position": v(-33.9, -5) * mm});
            skCircle(sketch, "E32", {"center": v(-33.9, -5) * mm, "radius": 3.3 * mm});
            skSolve(sketch);
        }
        {
            var Q0;
            Q0 = qSketchRegion(id + "F2", true);
            extrude(context, id + "F3", {"entities" : qUnion([Q0]), "operationType" : NewBodyOperationType.REMOVE, "endBound" : BoundingType.THROUGH_ALL, "oppositeDirection" : true, "depth" : 25 * mm});
        }
    });
